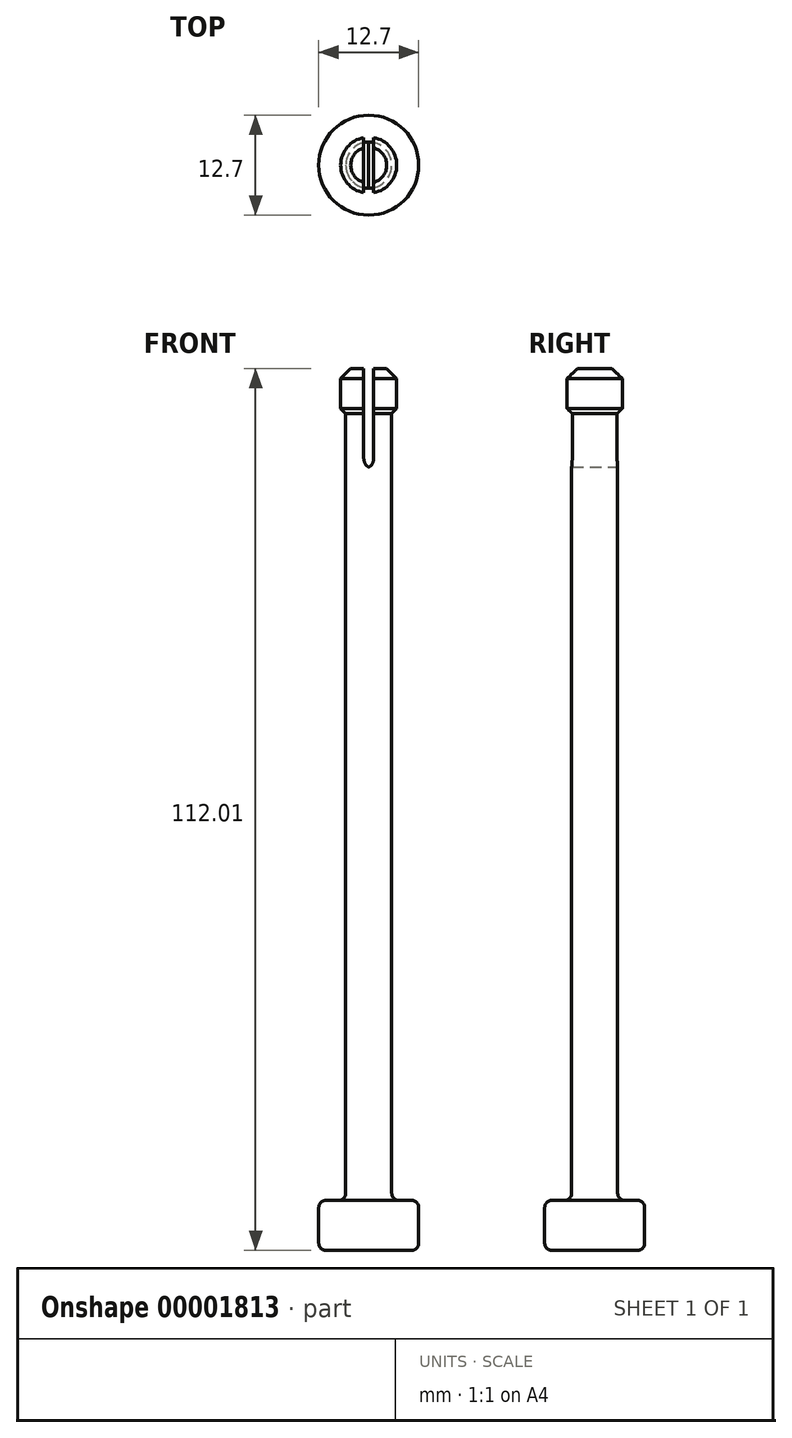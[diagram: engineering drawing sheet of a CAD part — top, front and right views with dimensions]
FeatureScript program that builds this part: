
annotation { "Feature Type Name" : "Feature", "Feature Type Description" : "" }
export const myFeature = defineFeature(function(context is Context, id is Id, definition is map)
    precondition{}
    {
        {
            var Q0;
            Q0=qCreatedBy(makeId("Front.planeOp"),FACE);
            var sketch = newSketch(context, id + "F0", { "sketchPlane" : qUnion([Q0])});
            skLineSegment(sketch, "E0", {"start": v(0, 0) * mm, "end": v(6.35, 0) * mm});
            skLineSegment(sketch, "E1", {"start": v(6.35, 0) * mm, "end": v(6.35, 6.35) * mm});
            skLineSegment(sketch, "E2", {"start": v(6.35, 6.35) * mm, "end": v(2.92, 6.35) * mm});
            skLineSegment(sketch, "E3", {"start": v(2.92, 6.35) * mm, "end": v(2.92, 105.66) * mm});
            skLineSegment(sketch, "E4", {"start": v(2.92, 105.66) * mm, "end": v(3.56, 105.66) * mm});
            skLineSegment(sketch, "E5", {"start": v(3.56, 105.66) * mm, "end": v(3.56, 112.01) * mm});
            skLineSegment(sketch, "E6", {"start": v(3.56, 112.01) * mm, "end": v(0, 112.01) * mm});
            skLineSegment(sketch, "E7", {"start": v(0, 112.01) * mm, "end": v(0, 0) * mm});
            skSolve(sketch);
        }
        {
            var Q0;
            Q0=makeQuery(id+"F0.imprint","IMPRINT",FACE,{"disambiguationData":[TD([[makeQuery(id+"F0.imprint","IMPRINT",EDGE,{"derivedFrom":sQuery(id+"F0.wireOp",EDGE,"E0")}),1.0]])]});
            var Q1;
            Q1=sQuery(id+"F0.wireOp",EDGE,"E7");
            revolve(context, id + "F1", {"entities" : qUnion([Q0]), "axis" : qUnion([Q1]), "revolveType" : RevolveType.FULL});
        }
        {
            var Q0;
            Q0=qCreatedBy(makeId("Front.planeOp"),FACE);
            var sketch = newSketch(context, id + "F2", { "sketchPlane" : qUnion([Q0])});
            skLineSegment(sketch, "E8.0", {"start": v(-3.56, 112.01) * mm, "end": v(3.56, 112.01) * mm});
            skLineSegment(sketch, "E9.rect.bottom", {"start": v(0.64, 99.31) * mm, "end": v(-0.63, 99.31) * mm});
            skLineSegment(sketch, "E9.rect.top", {"start": v(0.64, 124.71) * mm, "end": v(-0.63, 124.71) * mm});
            skLineSegment(sketch, "E9.rect.left", {"start": v(0.64, 99.31) * mm, "end": v(0.64, 124.71) * mm});
            skLineSegment(sketch, "E9.rect.right", {"start": v(-0.63, 99.31) * mm, "end": v(-0.63, 124.71) * mm});
            skPoint(sketch, "E9.rect.middle", {"position": v(0, 112.01) * mm});
            skSolve(sketch);
        }
        {
            var Q0;
            {var subQ3=sQuery(id+"F2.wireOp",EDGE,"E9.rect.bottom");Q0=makeQuery(id+"F2.imprint","IMPRINT",FACE,{"disambiguationData":[TD([[makeQuery(id+"F2.imprint","IMPRINT",EDGE,{"derivedFrom":subQ3}),-1.0]])]});}
            extrude(context, id + "F3", {"entities" : qUnion([Q0]), "operationType" : NewBodyOperationType.REMOVE, "endBound" : BoundingType.SYMMETRIC, "depth" : 25.4 * mm});
        }
        {
            var Q0;
            Q0=makeQuery(id+"F3.boolean.opBoolean","COPY",EDGE,{"derivedFrom":makeQuery(id+"F3.opExtrude","SWEPT_EDGE",EDGE,{"disambiguationData":[OSD([sQuery(id+"F2.wireOp",EDGE,"E9.rect.bottom"),sQuery(id+"F2.wireOp",EDGE,"E9.rect.left")])]})});
            var Q1;
            Q1=makeQuery(id+"F3.boolean.opBoolean","COPY",EDGE,{"derivedFrom":makeQuery(id+"F3.opExtrude","SWEPT_EDGE",EDGE,{"disambiguationData":[OSD([sQuery(id+"F2.wireOp",EDGE,"E9.rect.bottom"),sQuery(id+"F2.wireOp",EDGE,"E9.rect.right")])]})});
            fillet(context, id + "F4", {"entities" : qUnion([Q0, Q1]), "radius" : 1.27 * mm, "tangentPropagation" : true, "allowEdgeOverflow" : false});
        }
        {
            var Q0;
            {var subQ0=sQuery(id+"F0.wireOp",EDGE,"E5");var subQ1=sQuery(id+"F0.wireOp",EDGE,"E6");Q0=makeQuery(id+"F3.boolean.opBoolean","SPLIT",EDGE,{"disambiguationData":[TD([makeQuery(id+"F3.opExtrude","SWEPT_FACE",FACE,{"disambiguationData":[OSD([sQuery(id+"F2.wireOp",EDGE,"E9.rect.right")])]})])],"derivedFrom":makeQuery(id+"F1.opRevolve","SWEPT_EDGE",EDGE,{"disambiguationData":[OSD([subQ0,subQ1])]})});}
            var Q1;
            {var subQ0=sQuery(id+"F0.wireOp",EDGE,"E5");var subQ1=sQuery(id+"F0.wireOp",EDGE,"E6");Q1=makeQuery(id+"F3.boolean.opBoolean","SPLIT",EDGE,{"disambiguationData":[TD([makeQuery(id+"F3.opExtrude","SWEPT_FACE",FACE,{"disambiguationData":[OSD([sQuery(id+"F2.wireOp",EDGE,"E9.rect.left")])]})])],"derivedFrom":makeQuery(id+"F1.opRevolve","SWEPT_EDGE",EDGE,{"disambiguationData":[OSD([subQ0,subQ1])]})});}
            var Q2;
            {var subQ0=sQuery(id+"F0.wireOp",EDGE,"E4");var subQ1=sQuery(id+"F0.wireOp",EDGE,"E5");Q2=makeQuery(id+"F3.boolean.opBoolean","SPLIT",EDGE,{"disambiguationData":[TD([makeQuery(id+"F3.opExtrude","SWEPT_FACE",FACE,{"disambiguationData":[OSD([sQuery(id+"F2.wireOp",EDGE,"E9.rect.right")])]})])],"derivedFrom":makeQuery(id+"F1.opRevolve","SWEPT_EDGE",EDGE,{"disambiguationData":[OSD([subQ0,subQ1])]})});}
            var Q3;
            {var subQ0=sQuery(id+"F0.wireOp",EDGE,"E4");var subQ1=sQuery(id+"F0.wireOp",EDGE,"E5");Q3=makeQuery(id+"F3.boolean.opBoolean","SPLIT",EDGE,{"disambiguationData":[TD([makeQuery(id+"F3.opExtrude","SWEPT_FACE",FACE,{"disambiguationData":[OSD([sQuery(id+"F2.wireOp",EDGE,"E9.rect.left")])]})])],"derivedFrom":makeQuery(id+"F1.opRevolve","SWEPT_EDGE",EDGE,{"disambiguationData":[OSD([subQ0,subQ1])]})});}
            chamfer(context, id + "F5", {"entities" : qUnion([Q0, Q1, Q2, Q3]), "width" : 1.27 * mm, "tangentPropagation" : true});
        }
        {
            var Q0;
            Q0=makeQuery(id+"F1.opRevolve","SWEPT_EDGE",EDGE,{"disambiguationData":[OSD([sQuery(id+"F0.wireOp",EDGE,"E2"),sQuery(id+"F0.wireOp",EDGE,"E3")])]});
            var Q1;
            Q1=makeQuery(id+"F1.opRevolve","SWEPT_EDGE",EDGE,{"disambiguationData":[OSD([sQuery(id+"F0.wireOp",EDGE,"E1"),sQuery(id+"F0.wireOp",EDGE,"E2")])]});
            var Q2;
            Q2=makeQuery(id+"F1.opRevolve","SWEPT_EDGE",EDGE,{"disambiguationData":[OSD([sQuery(id+"F0.wireOp",EDGE,"E0"),sQuery(id+"F0.wireOp",EDGE,"E1")])]});
            fillet(context, id + "F6", {"entities" : qUnion([Q0, Q1, Q2]), "radius" : 0.89 * mm, "tangentPropagation" : true, "allowEdgeOverflow" : false});
        }
    });
